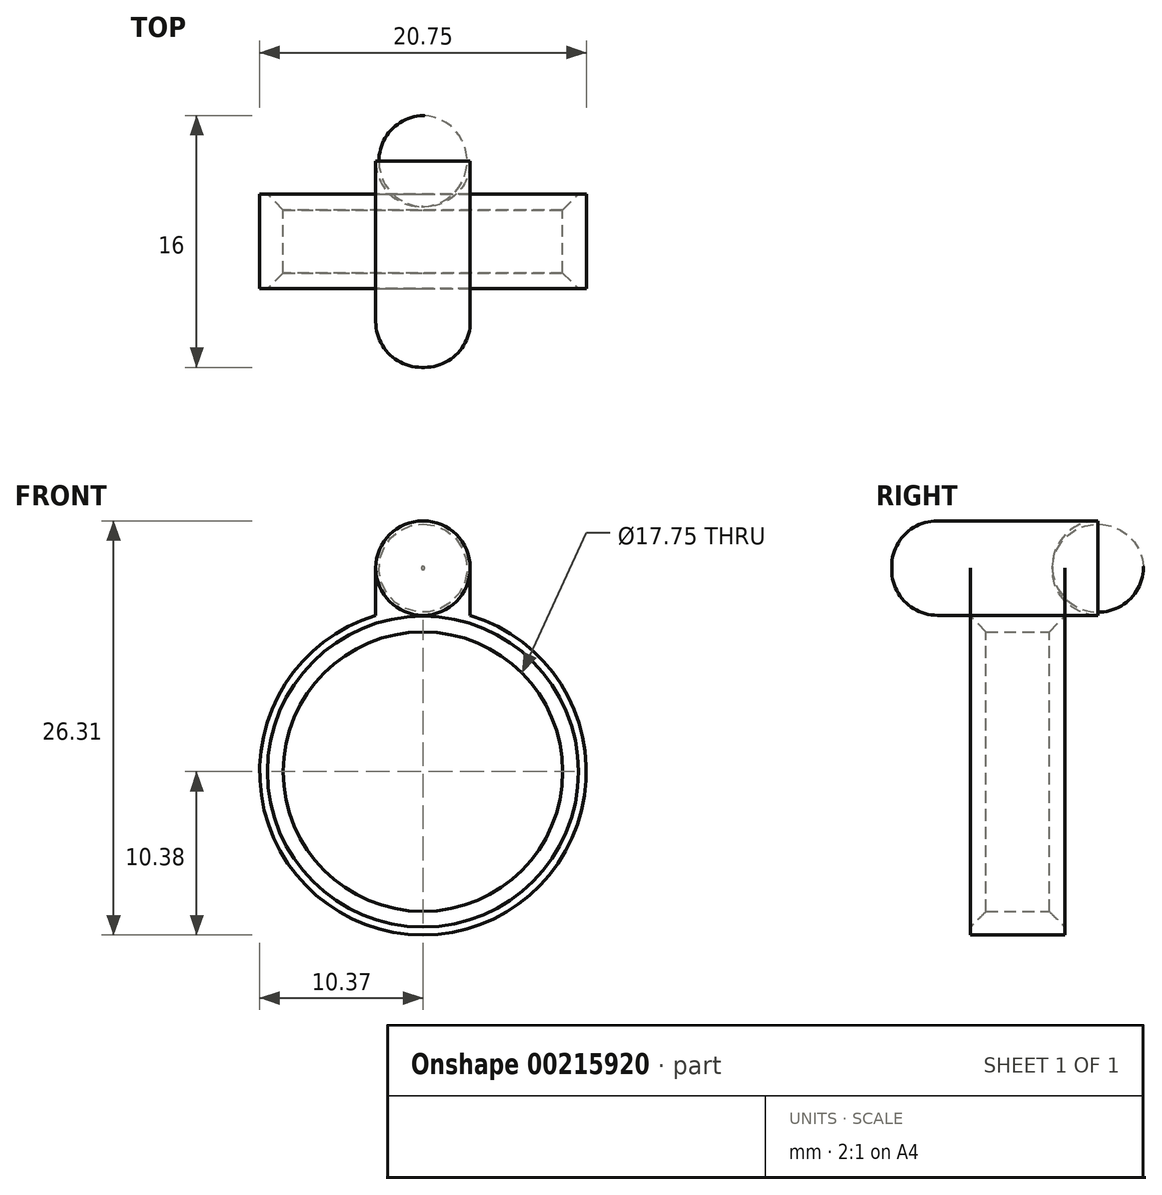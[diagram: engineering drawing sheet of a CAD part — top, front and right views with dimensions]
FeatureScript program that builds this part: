
annotation { "Feature Type Name" : "Feature", "Feature Type Description" : "" }
export const myFeature = defineFeature(function(context is Context, id is Id, definition is map)
    precondition{}
    {
        {
            var Q0;
            Q0=qCreatedBy(makeId("Front.planeOp"),FACE);
            var sketch = newSketch(context, id + "F0", { "sketchPlane" : qUnion([Q0])});
            skCircle(sketch, "E0", {"center": v(0, 0) * mm, "radius": 8.88 * mm});
            skCircle(sketch, "E1.0", {"center": v(0, 0) * mm, "radius": 10.38 * mm});
            skLineSegment(sketch, "E2.bottom", {"start": v(3, 9.93) * mm, "end": v(-3, 9.93) * mm});
            skLineSegment(sketch, "E2.top", {"start": v(3, 15.93) * mm, "end": v(-3, 15.93) * mm});
            skLineSegment(sketch, "E2.left", {"start": v(3, 9.93) * mm, "end": v(3, 15.93) * mm});
            skLineSegment(sketch, "E2.right", {"start": v(-3, 9.93) * mm, "end": v(-3, 15.93) * mm});
            skPoint(sketch, "E2.middle", {"position": v(0, 12.93) * mm});
            skSolve(sketch);
        }
        {
            var Q0;
            Q0=makeQuery(id+"F0.imprint","IMPRINT",FACE,{"disambiguationData":[TD([[makeQuery(id+"F0.imprint","IMPRINT",EDGE,{"derivedFrom":sQuery(id+"F0.wireOp",EDGE,"E0")}),-1.0]])]});
            var Q1;
            {var subQ0=sQuery(id+"F0.wireOp",EDGE,"6be46ea8-bbf3-414a-8f01-2c9cab33fd740.MirrorCS");var subQ1=sQuery(id+"F0.wireOp",EDGE,"E1.0");var subQ3=makeQuery(id+"F0.imprint","INTERSECT",VERTEX,{"derivedFrom":[subQ1,subQ0]});Q1=makeQuery(id+"F0.imprint","IMPRINT",FACE,{"disambiguationData":[TD([[makeQuery(id+"F0.imprint","IMPRINT",EDGE,{"disambiguationData":[TD([[subQ3,1.0]])],"derivedFrom":subQ1}),1.0]])]});}
            var Q2;
            {var subQ0=sQuery(id+"F0.wireOp",EDGE,"3nQ21Hy9-TuzR-lera-IFQC-aYX9ch6rXXm6");var subQ1=sQuery(id+"F0.wireOp",EDGE,"E1.0");var subQ3=makeQuery(id+"F0.imprint","INTERSECT",VERTEX,{"derivedFrom":[subQ1,subQ0]});Q2=makeQuery(id+"F0.imprint","IMPRINT",FACE,{"disambiguationData":[TD([[makeQuery(id+"F0.imprint","IMPRINT",EDGE,{"disambiguationData":[TD([[subQ3,-1.0]])],"derivedFrom":subQ1}),1.0]])]});}
            extrude(context, id + "F1", {"entities" : qUnion([Q0, Q1, Q2]), "depth" : 3 * mm, "hasSecondDirection" : true, "secondDirectionOppositeDirection" : true, "secondDirectionDepth" : 3 * mm});
        }
        {
            var Q0;
            Q0=makeQuery(id+"F1.opExtrude","CAP_EDGE",EDGE,{"disambiguationData":[OSD([sQuery(id+"F0.wireOp",EDGE,"E0")])],"isStart":false});
            var Q1;
            Q1=makeQuery(id+"F1.opExtrude","CAP_EDGE",EDGE,{"disambiguationData":[OSD([sQuery(id+"F0.wireOp",EDGE,"E0")])],"isStart":true});
            chamfer(context, id + "F2", {"entities" : qUnion([Q0, Q1]), "width" : 1 * mm, "tangentPropagation" : true});
        }
        {
            var Q0;
            Q0=makeQuery(id+"F0.imprint","IMPRINT",FACE,{"disambiguationData":[TD([[makeQuery(id+"F0.imprint","IMPRINT",EDGE,{"derivedFrom":sQuery(id+"F0.wireOp",EDGE,"E2.top")}),1.0]])]});
            var Q1;
            {var subQ0=sQuery(id+"F0.wireOp",EDGE,"E2.bottom");Q1=makeQuery(id+"F0.imprint","IMPRINT",FACE,{"disambiguationData":[TD([[makeQuery(id+"F0.imprint","IMPRINT",EDGE,{"derivedFrom":subQ0}),-1.0]])]});}
            extrude(context, id + "F3", {"entities" : qUnion([Q0, Q1]), "operationType" : NewBodyOperationType.ADD, "depth" : 8 * mm, "hasSecondDirection" : true, "secondDirectionOppositeDirection" : true, "secondDirectionDepth" : 8 * mm});
        }
        {
            var Q0;
            Q0=makeQuery(id+"F3.opExtrude","SWEPT_EDGE",EDGE,{"disambiguationData":[OSD([sQuery(id+"F0.wireOp",EDGE,"E2.top"),sQuery(id+"F0.wireOp",EDGE,"E2.right")])]});
            var Q1;
            Q1=makeQuery(id+"F3.opExtrude","SWEPT_EDGE",EDGE,{"disambiguationData":[OSD([sQuery(id+"F0.wireOp",EDGE,"E2.top"),sQuery(id+"F0.wireOp",EDGE,"E2.left")])]});
            var Q2;
            {var subQ0=sQuery(id+"F0.wireOp",EDGE,"E2.bottom");var subQ1=sQuery(id+"F0.wireOp",EDGE,"E1.0");var subQ2=sQuery(id+"F0.wireOp",EDGE,"E2.left");Q2=makeQuery(id+"F3.boolean.opBoolean","SPLIT",EDGE,{"disambiguationData":[TD([makeQuery(id+"F1.opExtrude","CAP_FACE",FACE,{"disambiguationData":[OSD([sQuery(id+"F0.wireOp",EDGE,"E0"),subQ1])],"isStart":false}),makeQuery(id+"F1.opExtrude","SWEPT_FACE",FACE,{"disambiguationData":[OSD([subQ1])]}),makeQuery(id+"F3.opExtrude","SWEPT_FACE",FACE,{"disambiguationData":[OSD([subQ0])]}),makeQuery(id+"F3.opExtrude","CAP_FACE",FACE,{"disambiguationData":[OSD([subQ0,sQuery(id+"F0.wireOp",EDGE,"E2.top"),subQ2,sQuery(id+"F0.wireOp",EDGE,"E2.right")])],"isStart":false}),makeQuery(id+"F3.opExtrude","SWEPT_FACE",FACE,{"disambiguationData":[OSD([subQ2])]})])],"derivedFrom":makeQuery(id+"F3.opExtrude","SWEPT_EDGE",EDGE,{"disambiguationData":[OSD([subQ1,subQ0,subQ2])]})});}
            var Q3;
            {var subQ0=sQuery(id+"F0.wireOp",EDGE,"E2.bottom");var subQ1=sQuery(id+"F0.wireOp",EDGE,"E1.0");var subQ2=sQuery(id+"F0.wireOp",EDGE,"E2.right");Q3=makeQuery(id+"F3.boolean.opBoolean","SPLIT",EDGE,{"disambiguationData":[TD([makeQuery(id+"F1.opExtrude","CAP_FACE",FACE,{"disambiguationData":[OSD([sQuery(id+"F0.wireOp",EDGE,"E0"),subQ1])],"isStart":false}),makeQuery(id+"F1.opExtrude","SWEPT_FACE",FACE,{"disambiguationData":[OSD([subQ1])]}),makeQuery(id+"F3.opExtrude","SWEPT_FACE",FACE,{"disambiguationData":[OSD([subQ0])]}),makeQuery(id+"F3.opExtrude","CAP_FACE",FACE,{"disambiguationData":[OSD([subQ0,sQuery(id+"F0.wireOp",EDGE,"E2.top"),sQuery(id+"F0.wireOp",EDGE,"E2.left"),subQ2])],"isStart":false}),makeQuery(id+"F3.opExtrude","SWEPT_FACE",FACE,{"disambiguationData":[OSD([subQ2])]})])],"derivedFrom":makeQuery(id+"F3.opExtrude","SWEPT_EDGE",EDGE,{"disambiguationData":[OSD([subQ1,subQ0,subQ2])]})});}
            var Q4;
            {var subQ0=sQuery(id+"F0.wireOp",EDGE,"E2.bottom");var subQ1=sQuery(id+"F0.wireOp",EDGE,"E1.0");var subQ2=sQuery(id+"F0.wireOp",EDGE,"E2.left");Q4=makeQuery(id+"F3.boolean.opBoolean","SPLIT",EDGE,{"disambiguationData":[TD([makeQuery(id+"F1.opExtrude","CAP_FACE",FACE,{"disambiguationData":[OSD([sQuery(id+"F0.wireOp",EDGE,"E0"),subQ1])],"isStart":true}),makeQuery(id+"F1.opExtrude","SWEPT_FACE",FACE,{"disambiguationData":[OSD([subQ1])]}),makeQuery(id+"F3.opExtrude","SWEPT_FACE",FACE,{"disambiguationData":[OSD([subQ0])]}),makeQuery(id+"F3.opExtrude","CAP_FACE",FACE,{"disambiguationData":[OSD([subQ0,sQuery(id+"F0.wireOp",EDGE,"E2.top"),subQ2,sQuery(id+"F0.wireOp",EDGE,"E2.right")])],"isStart":true}),makeQuery(id+"F3.opExtrude","SWEPT_FACE",FACE,{"disambiguationData":[OSD([subQ2])]})])],"derivedFrom":makeQuery(id+"F3.opExtrude","SWEPT_EDGE",EDGE,{"disambiguationData":[OSD([subQ1,subQ0,subQ2])]})});}
            var Q5;
            {var subQ0=sQuery(id+"F0.wireOp",EDGE,"E2.bottom");var subQ1=sQuery(id+"F0.wireOp",EDGE,"E1.0");var subQ2=sQuery(id+"F0.wireOp",EDGE,"E2.right");Q5=makeQuery(id+"F3.boolean.opBoolean","SPLIT",EDGE,{"disambiguationData":[TD([makeQuery(id+"F1.opExtrude","CAP_FACE",FACE,{"disambiguationData":[OSD([sQuery(id+"F0.wireOp",EDGE,"E0"),subQ1])],"isStart":true}),makeQuery(id+"F1.opExtrude","SWEPT_FACE",FACE,{"disambiguationData":[OSD([subQ1])]}),makeQuery(id+"F3.opExtrude","SWEPT_FACE",FACE,{"disambiguationData":[OSD([subQ0])]}),makeQuery(id+"F3.opExtrude","CAP_FACE",FACE,{"disambiguationData":[OSD([subQ0,sQuery(id+"F0.wireOp",EDGE,"E2.top"),sQuery(id+"F0.wireOp",EDGE,"E2.left"),subQ2])],"isStart":true}),makeQuery(id+"F3.opExtrude","SWEPT_FACE",FACE,{"disambiguationData":[OSD([subQ2])]})])],"derivedFrom":makeQuery(id+"F3.opExtrude","SWEPT_EDGE",EDGE,{"disambiguationData":[OSD([subQ1,subQ0,subQ2])]})});}
            fillet(context, id + "F4", {"entities" : qUnion([Q0, Q1, Q2, Q3, Q4, Q5]), "radius" : 3 * mm, "tangentPropagation" : true, "allowEdgeOverflow" : false});
        }
        {
            var Q0;
            {var subQ0=sQuery(id+"F0.wireOp",EDGE,"E2.left");var subQ1=sQuery(id+"F0.wireOp",EDGE,"E2.top");Q0=makeQuery(id+"F4.opFillet","BLEND_EDGE",EDGE,{"blendedFrom":[makeQuery(id+"F3.opExtrude","SWEPT_EDGE",EDGE,{"disambiguationData":[OSD([subQ1,subQ0])]}),makeQuery(id+"F3.opExtrude","CAP_FACE",FACE,{"disambiguationData":[OSD([sQuery(id+"F0.wireOp",EDGE,"E2.bottom"),subQ1,subQ0,sQuery(id+"F0.wireOp",EDGE,"E2.right")])],"isStart":false})],"blendedInto":[makeQuery(id+"F3.opExtrude","CAP_FACE",FACE,{"disambiguationData":[OSD([sQuery(id+"F0.wireOp",EDGE,"E2.bottom"),subQ1,subQ0,sQuery(id+"F0.wireOp",EDGE,"E2.right")])],"isStart":false})]});}
            var Q1;
            {var subQ0=sQuery(id+"F0.wireOp",EDGE,"E2.left");var subQ1=sQuery(id+"F0.wireOp",EDGE,"E2.top");Q1=makeQuery(id+"F4.opFillet","BLEND_EDGE",EDGE,{"blendedFrom":[makeQuery(id+"F3.opExtrude","SWEPT_EDGE",EDGE,{"disambiguationData":[OSD([subQ1,subQ0])]}),makeQuery(id+"F3.opExtrude","CAP_FACE",FACE,{"disambiguationData":[OSD([sQuery(id+"F0.wireOp",EDGE,"E2.bottom"),subQ1,subQ0,sQuery(id+"F0.wireOp",EDGE,"E2.right")])],"isStart":true})],"blendedInto":[makeQuery(id+"F3.opExtrude","CAP_FACE",FACE,{"disambiguationData":[OSD([sQuery(id+"F0.wireOp",EDGE,"E2.bottom"),subQ1,subQ0,sQuery(id+"F0.wireOp",EDGE,"E2.right")])],"isStart":true})]});}
            fillet(context, id + "F5", {"entities" : qUnion([Q0, Q1]), "radius" : 2.9 * mm, "tangentPropagation" : true, "allowEdgeOverflow" : false});
        }
    });
